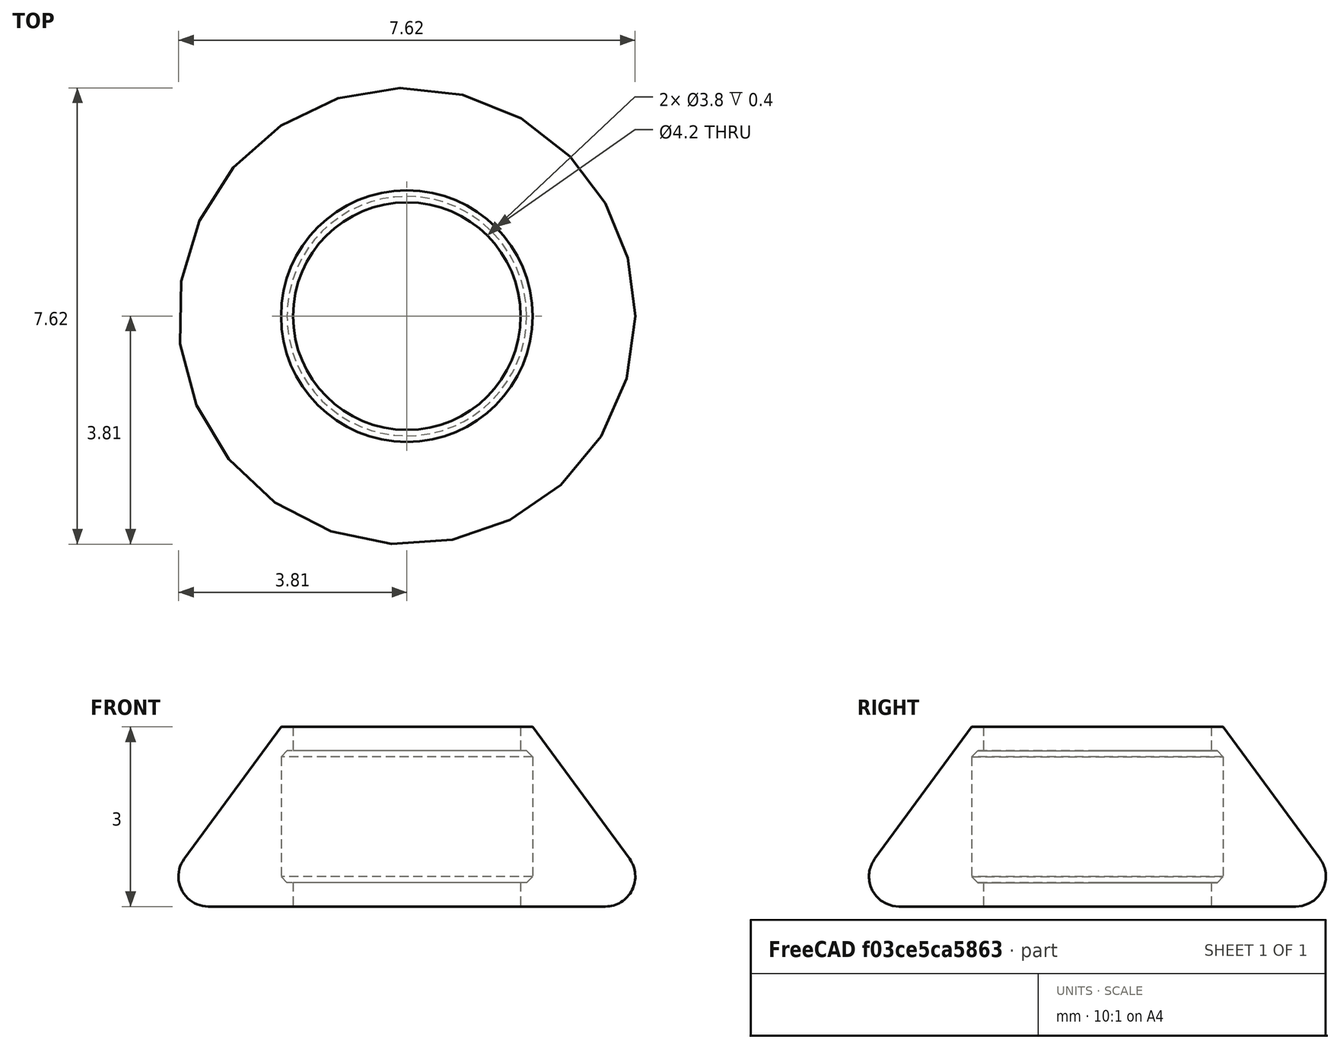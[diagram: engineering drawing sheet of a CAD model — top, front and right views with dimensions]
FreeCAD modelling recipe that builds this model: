
FCSTD DOCUMENT  (FreeCAD 0.18.4R)
Label: ScrewHoleGasket
License: All rights reserved
LicenseURL: http://en.wikipedia.org/wiki/All_rights_reserved
objects: Part::Cylinder×4, Part::MultiFuse×2, Part::Cut×2, Part::Chamfer×2, Part::Cone×1, Part::Fillet×1, Mesh::Feature×1
note: 12 computed .brp shape members not serialized (recipe doc carries the construction recipe); baked Part::Feature solids carry a one-line shape summary decoded from their .brp

FEATURE [Part::Cone] Cone  label="Kegel"
  Angle = 360
  AttacherType = Attacher::AttachEngine3D
  Height = 3
  Radius1 = 2.1
  Radius2 = 4.3
FEATURE [Part::Cylinder] Cylinder  label="Zylinder"
  Angle = 360
  AttacherType = Attacher::AttachEngine3D
  Height = 10
  Placement = pos=(0,0,-2) rot=(0,0,1;0rad)
  Radius = 2.1
FEATURE [Part::Cylinder] Cylinder001  label="Zylinder001"
  Angle = 360
  AttacherType = Attacher::AttachEngine3D
  Height = 0.4
  Radius = 2.1
FEATURE [Part::Cylinder] Cylinder002  label="Zylinder002"
  Angle = 360
  AttacherType = Attacher::AttachEngine3D
  Height = 0.4
  Placement = pos=(0,0,2.6) rot=(0,0,1;0rad)
  Radius = 2.1
FEATURE [Part::MultiFuse] Fusion
  Shapes = -> [Cylinder002,Cylinder001]
FEATURE [Part::Cylinder] Cylinder003  label="Zylinder003"
  Angle = 360
  AttacherType = Attacher::AttachEngine3D
  Height = 10
  Placement = pos=(0,0,-3) rot=(0,0,1;0rad)
  Radius = 1.9
FEATURE [Part::Cut] Cut
  Base = -> Cone
  Tool = -> Cylinder
FEATURE [Part::Cut] Cut001
  Base = -> Fusion
  Tool = -> Cylinder003
FEATURE [Part::MultiFuse] Fusion001
  Shapes = -> [Cut,Cut001]
FEATURE [Part::Chamfer] Chamfer
  Base = -> Fusion001
  Edges = 1 edges r=0.1: [Edge5]
FEATURE [Part::Chamfer] Chamfer001
  Base = -> Chamfer
  Edges = 1 edges r=0.1: [Edge8]
FEATURE [Part::Fillet] Fillet
  Base = -> Chamfer001
  Edges = 1 edges r=0.5: [Edge17]
  Placement = pos=(0,0,0) rot=(1,0,0;3.14159rad)
FEATURE [Mesh::Feature] Mesh  label="Fillet (Meshed)"
